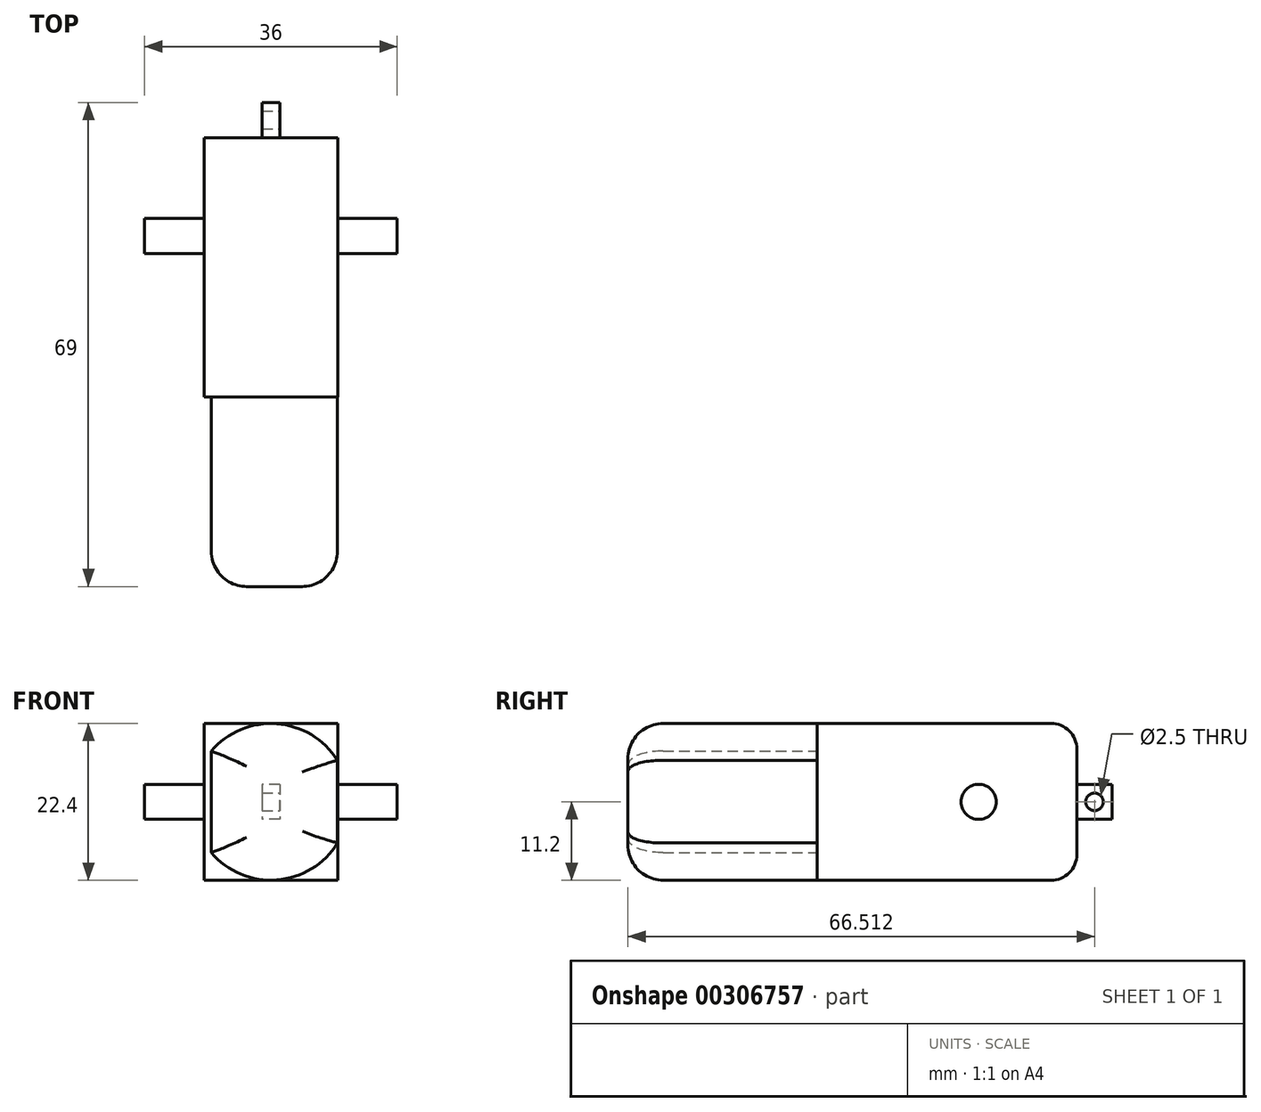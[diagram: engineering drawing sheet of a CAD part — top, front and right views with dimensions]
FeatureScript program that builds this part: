
annotation { "Feature Type Name" : "Feature", "Feature Type Description" : "" }
export const myFeature = defineFeature(function(context is Context, id is Id, definition is map)
    precondition{}
    {
        {
            var Q0;
            Q0=qCreatedBy(makeId("Right.planeOp"),FACE);
            var sketch = newSketch(context, id + "F0", { "sketchPlane" : qUnion([Q0])});
            skLineSegment(sketch, "E0.bottom", {"start": v(-18.5, 11.2) * mm, "end": v(18.5, 11.2) * mm});
            skLineSegment(sketch, "E0.top", {"start": v(-18.5, -11.2) * mm, "end": v(18.5, -11.2) * mm});
            skLineSegment(sketch, "E0.left", {"start": v(-18.5, 11.2) * mm, "end": v(-18.5, -11.2) * mm});
            skLineSegment(sketch, "E0.right", {"start": v(18.5, 11.2) * mm, "end": v(18.5, -11.2) * mm});
            skSolve(sketch);
        }
        {
            var Q0;
            Q0 = qSketchRegion(id + "F0", true);
            extrude(context, id + "F1", {"entities" : qUnion([Q0]), "depth" : 19 * mm, "symmetric" : true});
        }
        {
            var Q0;
            Q0=makeQuery(id+"F1.opExtrude","SWEPT_EDGE",EDGE,{"disambiguationData":[OSD([sQuery(id+"F0.wireOp",EDGE,"E0.bottom"),sQuery(id+"F0.wireOp",EDGE,"E0.right")])]});
            var Q1;
            Q1=makeQuery(id+"F1.opExtrude","SWEPT_EDGE",EDGE,{"disambiguationData":[OSD([sQuery(id+"F0.wireOp",EDGE,"E0.top"),sQuery(id+"F0.wireOp",EDGE,"E0.right")])]});
            fillet(context, id + "F2", {"entities" : qUnion([Q0, Q1]), "radius" : 3.7 * mm, "tangentPropagation" : true, "allowEdgeOverflow" : false});
        }
        {
            var Q0;
            Q0=makeQuery(id+"F1.opExtrude","SWEPT_FACE",FACE,{"disambiguationData":[OSD([sQuery(id+"F0.wireOp",EDGE,"E0.right")])]});
            var sketch = newSketch(context, id + "F3", { "sketchPlane" : qUnion([Q0])});
            skLineSegment(sketch, "E1.bottom", {"start": v(-1.25, 2.5) * mm, "end": v(1.25, 2.5) * mm});
            skLineSegment(sketch, "E1.top", {"start": v(-1.25, -2.5) * mm, "end": v(1.25, -2.5) * mm});
            skLineSegment(sketch, "E1.left", {"start": v(-1.25, 2.5) * mm, "end": v(-1.25, -2.5) * mm});
            skLineSegment(sketch, "E1.right", {"start": v(1.25, 2.5) * mm, "end": v(1.25, -2.5) * mm});
            skSolve(sketch);
        }
        {
            var Q0;
            Q0=makeQuery(id+"F3.imprint","IMPRINT",FACE,{"disambiguationData":[TD([[makeQuery(id+"F3.imprint","IMPRINT",EDGE,{"derivedFrom":sQuery(id+"F3.wireOp",EDGE,"E1.bottom")}),-1.0]])]});
            extrude(context, id + "F4", {"entities" : qUnion([Q0]), "operationType" : NewBodyOperationType.ADD, "depth" : 5 * mm});
        }
        {
            var Q0;
            Q0=makeQuery(id+"F4.opExtrude","SWEPT_FACE",FACE,{"disambiguationData":[OSD([sQuery(id+"F3.wireOp",EDGE,"E1.left")])]});
            var sketch = newSketch(context, id + "F5", { "sketchPlane" : qUnion([Q0])});
            skCircle(sketch, "E2", {"center": v(21.01, 0) * mm, "radius": 1.25 * mm});
            skSolve(sketch);
        }
        {
            var Q0;
            Q0=makeQuery(id+"F5.imprint","IMPRINT",FACE,{"disambiguationData":[TD([[makeQuery(id+"F5.imprint","IMPRINT",EDGE,{"derivedFrom":sQuery(id+"F5.wireOp",EDGE,"E2")}),1.0]])]});
            extrude(context, id + "F6", {"entities" : qUnion([Q0]), "operationType" : NewBodyOperationType.REMOVE, "endBound" : BoundingType.THROUGH_ALL, "oppositeDirection" : true, "depth" : 25 * mm});
        }
        {
            var Q0;
            Q0=makeQuery(id+"F1.opExtrude","SWEPT_FACE",FACE,{"disambiguationData":[OSD([sQuery(id+"F0.wireOp",EDGE,"E0.left")])]});
            var sketch = newSketch(context, id + "F7", { "sketchPlane" : qUnion([Q0])});
            skLineSegment(sketch, "E3", {"start": v(-8.5, 7.24) * mm, "end": v(-8.5, -7.24) * mm});
            skArc(sketch, "E4", {"start": v(-8.5, -7.24) * mm, "mid": v(0.85, -11.13) * mm, "end": v(9.5, -5.87) * mm});
            skArc(sketch, "E5", {"start": v(9.46, 5.92) * mm, "mid": v(0.82, 11.13) * mm, "end": v(-8.5, 7.24) * mm});
            skLineSegment(sketch, "E6", {"start": v(9.46, 5.92) * mm, "end": v(9.5, -5.87) * mm});
            skSolve(sketch);
        }
        {
            var Q0;
            Q0 = qSketchRegion(id + "F7", true);
            extrude(context, id + "F8", {"entities" : qUnion([Q0]), "operationType" : NewBodyOperationType.ADD, "depth" : 27 * mm});
        }
        {
            var Q0;
            Q0=makeQuery(id+"F8.opExtrude","CAP_FACE",FACE,{"disambiguationData":[OSD([sQuery(id+"F7.wireOp",EDGE,"E3"),sQuery(id+"F7.wireOp",EDGE,"E4"),sQuery(id+"F7.wireOp",EDGE,"E5"),sQuery(id+"F7.wireOp",EDGE,"E6")])],"isStart":false});
            fillet(context, id + "F9", {"entities" : qUnion([Q0]), "radius" : 5 * mm, "tangentPropagation" : true, "allowEdgeOverflow" : false});
        }
        {
            var Q0;
            Q0=makeQuery(id+"F1.opExtrude","CAP_FACE",FACE,{"disambiguationData":[OSD([sQuery(id+"F0.wireOp",EDGE,"E0.bottom"),sQuery(id+"F0.wireOp",EDGE,"E0.top"),sQuery(id+"F0.wireOp",EDGE,"E0.left"),sQuery(id+"F0.wireOp",EDGE,"E0.right")])],"isStart":false});
            var sketch = newSketch(context, id + "F10", { "sketchPlane" : qUnion([Q0])});
            skCircle(sketch, "E7", {"center": v(4.5, 0) * mm, "radius": 2.5 * mm});
            skLineSegment(sketch, "E8", {"start": v(7, 0) * mm, "end": v(18.5, 0) * mm, "construction": true});
            skSolve(sketch);
        }
        {
            var Q0;
            Q0 = qSketchRegion(id + "F10", true);
            extrude(context, id + "F11", {"entities" : qUnion([Q0]), "depth" : 8.5 * mm});
        }
        {
            var Q0;
            Q0=makeQuery(id+"F11.opExtrude","SWEPT_BODY",BODY,{"disambiguationData":[OSD([sQuery(id+"F10.wireOp",EDGE,"E7")])]});
            var Q1;
            Q1=qCreatedBy(makeId("Right.planeOp"),FACE);
            mirror(context, id + "F12", {"operationType" : NewBodyOperationType.ADD, "entities" : qUnion([Q0]), "mirrorPlane" : qUnion([Q1])});
        }
    });
